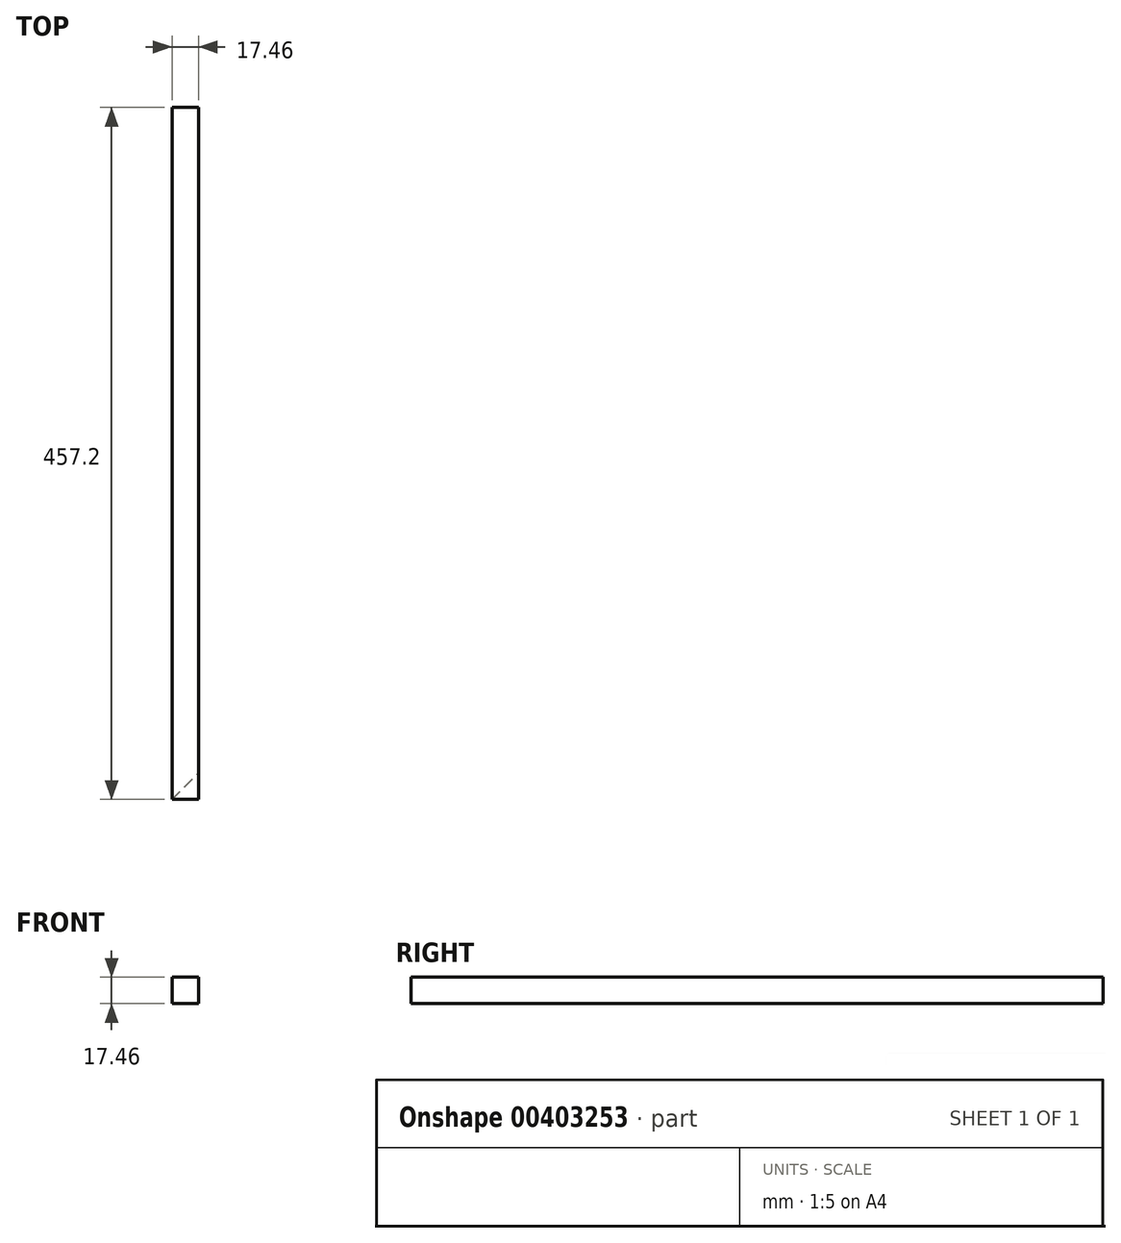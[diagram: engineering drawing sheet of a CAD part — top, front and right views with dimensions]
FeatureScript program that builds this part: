
annotation { "Feature Type Name" : "Feature", "Feature Type Description" : "" }
export const myFeature = defineFeature(function(context is Context, id is Id, definition is map)
    precondition{}
    {
        {
            var Q0;
            Q0=qCreatedBy(makeId("Front.planeOp"),FACE);
            var sketch = newSketch(context, id + "F0", { "sketchPlane" : qUnion([Q0])});
            skLineSegment(sketch, "E0.bottom", {"start": v(-8.73, -8.73) * mm, "end": v(8.73, -8.73) * mm});
            skLineSegment(sketch, "E0.top", {"start": v(-8.73, 8.73) * mm, "end": v(8.73, 8.73) * mm});
            skLineSegment(sketch, "E0.left", {"start": v(-8.73, -8.73) * mm, "end": v(-8.73, 8.73) * mm});
            skLineSegment(sketch, "E0.right", {"start": v(8.73, -8.73) * mm, "end": v(8.73, 8.73) * mm});
            skSolve(sketch);
        }
        {
            var Q0;
            Q0=makeQuery(id+"F0.imprint","IMPRINT",FACE,{"disambiguationData":[TD([[makeQuery(id+"F0.imprint","IMPRINT",EDGE,{"derivedFrom":sQuery(id+"F0.wireOp",EDGE,"E0.bottom")}),1.0]])]});
            extrude(context, id + "F1", {"entities" : qUnion([Q0]), "depth" : 457.2 * mm});
        }
        {
            var Q0;
            Q0=makeQuery(id+"F1.opExtrude","SWEPT_FACE",FACE,{"disambiguationData":[OSD([sQuery(id+"F0.wireOp",EDGE,"E0.bottom")])]});
            var sketch = newSketch(context, id + "F2", { "sketchPlane" : qUnion([Q0])});
            skLineSegment(sketch, "E1", {"start": v(-8.73, 457.2) * mm, "end": v(8.73, 439.74) * mm});
            skLineSegment(sketch, "E2", {"start": v(8.73, 439.74) * mm, "end": v(8.73, 457.2) * mm});
            skLineSegment(sketch, "E3", {"start": v(8.73, 457.2) * mm, "end": v(-8.73, 457.2) * mm});
            skSolve(sketch);
        }
        {
            var Q0;
            Q0=makeQuery(id+"F2.imprint","IMPRINT",FACE,{"disambiguationData":[TD([[makeQuery(id+"F2.imprint","IMPRINT",EDGE,{"derivedFrom":sQuery(id+"F2.wireOp",EDGE,"E1")}),1.0]])]});
            extrude(context, id + "F3", {"entities" : qUnion([Q0]), "operationType" : NewBodyOperationType.REMOVE, "oppositeDirection" : true, "depth" : 11 / 406.4 * mm});
        }
    });
